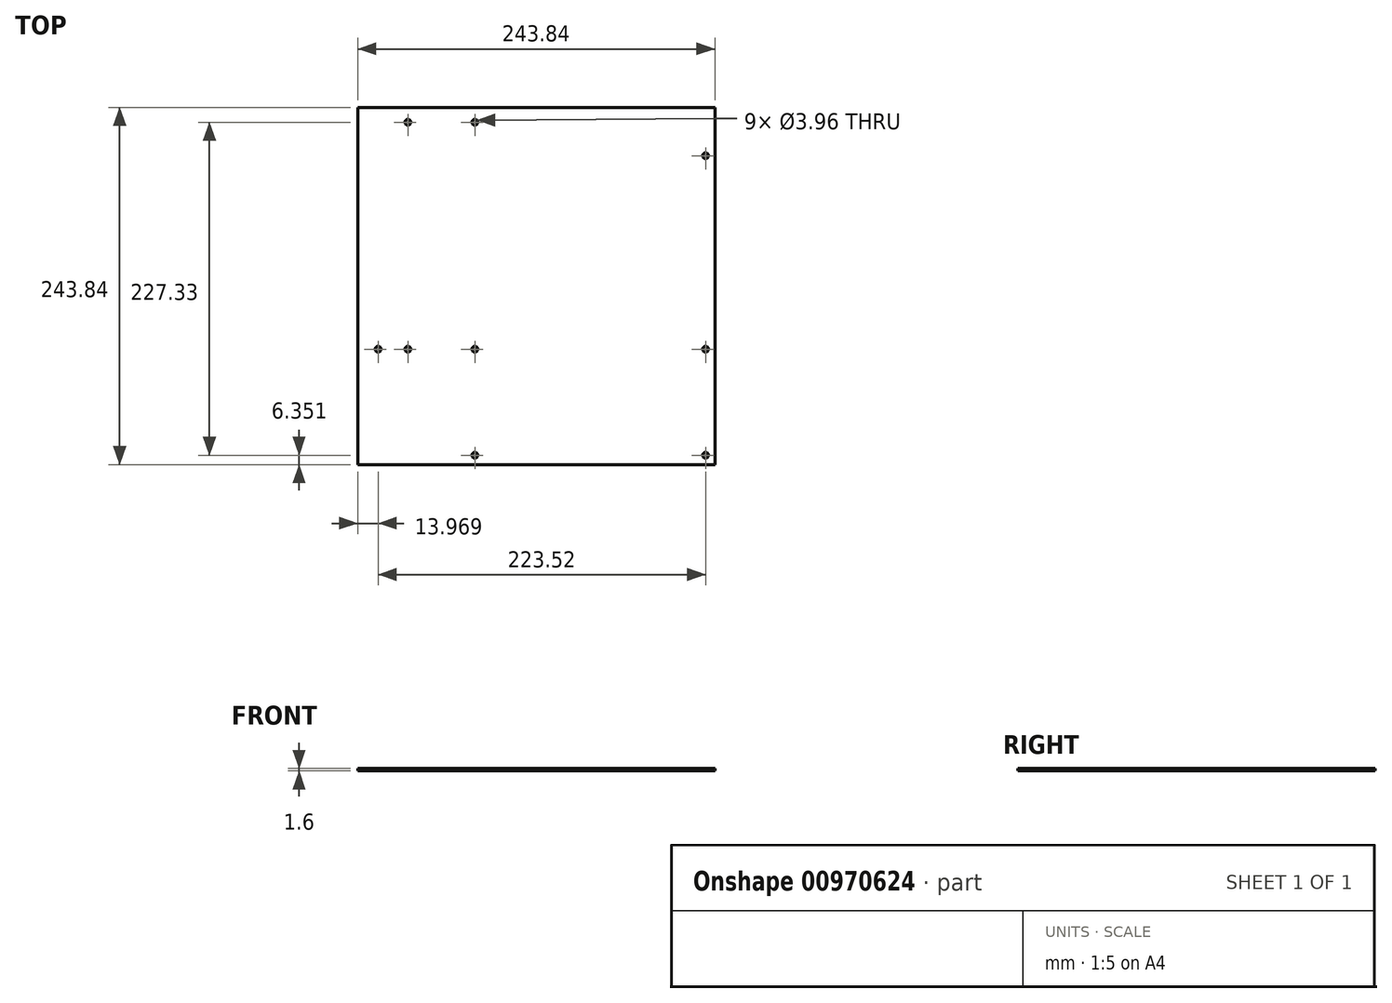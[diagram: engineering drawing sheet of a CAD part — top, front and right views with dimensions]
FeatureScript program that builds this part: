
annotation { "Feature Type Name" : "Feature", "Feature Type Description" : "" }
export const myFeature = defineFeature(function(context is Context, id is Id, definition is map)
    precondition{}
    {
        {
            var Q0;
            Q0=qCreatedBy(makeId("Top.planeOp"),FACE);
            var sketch = newSketch(context, id + "F0", { "sketchPlane" : qUnion([Q0])});
            skLineSegment(sketch, "E0.bottom", {"start": v(-125.8, 120.75) * mm, "end": v(118.04, 120.75) * mm});
            skLineSegment(sketch, "E0.top", {"start": v(-125.8, -123.09) * mm, "end": v(118.04, -123.09) * mm});
            skLineSegment(sketch, "E0.left", {"start": v(-125.8, 120.75) * mm, "end": v(-125.8, -123.09) * mm});
            skLineSegment(sketch, "E0.right", {"start": v(118.04, 120.75) * mm, "end": v(118.04, -123.09) * mm});
            skCircle(sketch, "E1", {"center": v(-91.51, 110.6) * mm, "radius": 1.98 * mm});
            skCircle(sketch, "E2", {"center": v(-45.8, 110.6) * mm, "radius": 1.98 * mm});
            skCircle(sketch, "E3", {"center": v(-91.51, -44.35) * mm, "radius": 1.98 * mm});
            skCircle(sketch, "E4", {"center": v(-111.83, -44.35) * mm, "radius": 1.98 * mm});
            skCircle(sketch, "E5", {"center": v(-45.8, -44.35) * mm, "radius": 1.98 * mm});
            skCircle(sketch, "E6", {"center": v(-45.8, -116.74) * mm, "radius": 1.98 * mm});
            skCircle(sketch, "E7", {"center": v(111.69, -116.74) * mm, "radius": 1.98 * mm});
            skCircle(sketch, "E8", {"center": v(111.69, -44.35) * mm, "radius": 1.98 * mm});
            skCircle(sketch, "E9", {"center": v(111.69, 87.73) * mm, "radius": 1.98 * mm});
            skSolve(sketch);
        }
        {
            var Q0;
            Q0=makeQuery(id+"F0.imprint","IMPRINT",FACE,{"disambiguationData":[TD([[makeQuery(id+"F0.imprint","IMPRINT",EDGE,{"derivedFrom":sQuery(id+"F0.wireOp",EDGE,"E0.bottom")}),-1.0]])]});
            extrude(context, id + "F1", {"entities" : qUnion([Q0]), "depth" : 1.6 * mm, "offsetDistance" : 25 * mm});
        }
    });
